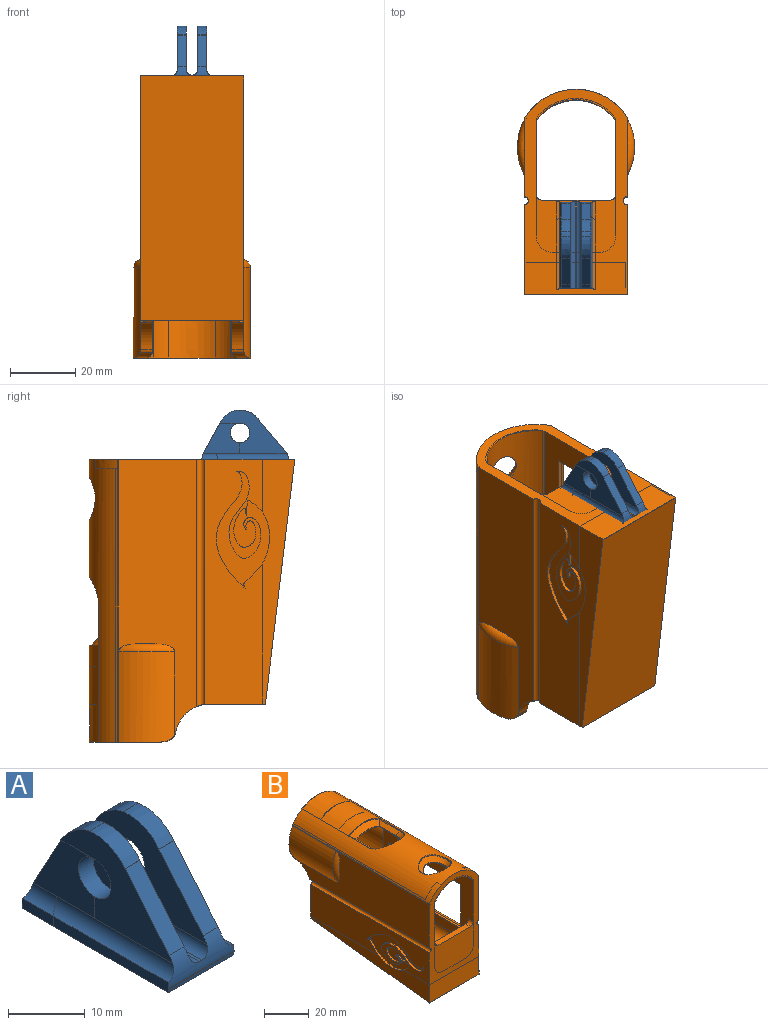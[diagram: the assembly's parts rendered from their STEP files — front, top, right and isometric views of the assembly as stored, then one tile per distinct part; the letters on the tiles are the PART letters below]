
ASSEMBLY  parts=2 mates=1
PART A: 46 faces, bbox 12.1x27.6x17 mm
  f0: extruded ~12.04x3.57mm, area 34.1mm2, adj f5,f6,f8,f10,f11,f12,f13,f14
  f1: plane 20.62x13.45mm, normal (-1,0,0), area 121.6mm2, adj f7,f8,f15,f16,f17,f22,f24,f28
  f2: plane 21.84x13.45mm, normal (1,0,0), area 173.4mm2, adj f9,f18,f20,f22,f23,f29,f30,f35
  f3: plane 23.73x13.5mm, normal (1,0,0), area 180.6mm2, adj f5,f15,f16,f17,f22,f24,f26,f31
  f4: plane 23.73x13.5mm, normal (-1,0,0), area 180.6mm2, adj f6,f18,f22,f23,f25,f29,f30,f35
  f5: bspline ~5x3.72mm, area 10.4mm2, adj f0,f3,f26,f41
  f6: bspline ~5x4.09mm, area 10.4mm2, adj f0,f4,f25,f40
  f7: plane 5.68x0mm, normal (0,0,-1), area 0mm2, adj f1,f8,f15,f42
  f8: plane 11.28x9.4mm, normal (-1,0,0), area 68.2mm2, adj f0,f1,f7,f14,f15,f28,f36,f41
  f9: plane 7.19x4.21mm, normal (1,0,0), area 16.3mm2, adj f2,f39,f40
  f10: plane 5.82x1.62mm, normal (1,0,0), area 9.3mm2, adj f0,f11,f12,f32,f39
  f11: plane 27.2x12.05mm, normal (0,0,-1), area 327.5mm2, adj f0,f10,f12,f13,f19,f32,f33,f37
  f12: cylinder r=10mm len=1.15mm, axis (0,0,1), area 0.4mm2, adj f0,f10,f11
  f13: cylinder r=10mm len=1.16mm, axis (0,0,-1), area 0.4mm2, adj f0,f11,f37
  f14: plane 4.2x0mm, normal (0,0,1), area 0mm2, adj f0,f8,f38
  f15: cylinder r=3mm len=6mm, axis (-1,0,0), area 51.8mm2, adj f1,f3,f7,f8,f36
  f16: extruded ~6.58x2.75mm, area 20.5mm2, adj f1,f3,f17,f44
  f17: plane 2.75x0.01mm, normal (0,-0.61,-0.8), area 0mm2, adj f1,f3,f16,f31
  f18: plane 2.75x0.01mm, normal (0,-0.61,-0.8), area 0mm2, adj f2,f4,f29,f35
  f19: cylinder r=5mm len=12.05mm, axis (-1,0,0), area 6mm2, adj f11,f21,f32,f33
  f20: cylinder r=2mm len=22.15mm, axis (0,-1,0), area 57mm2, adj f2,f22,f32,f39
  f21: plane 12.05x0.16mm, normal (0,-1,0), area 2mm2, adj f19,f22,f32,f33
  f22: cylinder r=6mm len=12.05mm, axis (1,0,0), area 33.2mm2, adj f1,f2,f3,f4,f20,f21,f23,f24
  f23: plane 9.73x8.15mm, normal (0,-0.77,0.64), area 34.9mm2, adj f2,f4,f22,f29
  f24: plane 9.73x8.15mm, normal (0,-0.77,0.64), area 34.9mm2, adj f1,f3,f22,f31
  f25: cylinder r=1.5mm len=26.67mm, axis (0,1,0), area 61.7mm2, adj f0,f4,f6,f22,f27,f34
  f26: cylinder r=1.5mm len=26.67mm, axis (0,1,0), area 61.7mm2, adj f0,f3,f5,f22,f27,f34
  f27: plane 22.48x0.5mm, normal (0,0,1), area 11.2mm2, adj f22,f25,f26,f34
  f28: cylinder r=2mm len=22.14mm, axis (0,1,0), area 56.7mm2, adj f1,f8,f22,f33,f38
  f29: plane 2.75x0.02mm, normal (0,0,1), area 0mm2, adj f2,f4,f18,f23
  f30: cylinder r=3mm len=6mm, axis (-1,0,0), area 51.8mm2, adj f2,f4
  f31: plane 2.75x0.02mm, normal (0,0,1), area 0mm2, adj f1,f3,f17,f24
  f32: plane 21.18x1.61mm, normal (1,0,0), area 34.1mm2, adj f10,f11,f19,f20,f21,f22
  f33: plane 21.18x1.62mm, normal (-1,0,0), area 34.1mm2, adj f11,f19,f21,f22,f28,f37
  f34: bspline ~5x0.5mm, area 2.1mm2, adj f0,f25,f26,f27
  f35: extruded ~6.58x2.75mm, area 20.5mm2, adj f2,f4,f18,f45
  f36: plane 3.31x0mm, normal (0,1,0), area 0mm2, adj f1,f8,f15
  f37: plane 5.82x1.62mm, normal (-1,0,0), area 9.3mm2, adj f0,f11,f13,f33,f38
  f38: cylinder r=2mm len=5.73mm, axis (0,-1,0), area 13.2mm2, adj f0,f14,f28,f37
  f39: cylinder r=2mm len=5.72mm, axis (0,-1,0), area 12.8mm2, adj f0,f9,f10,f20
  f40: plane 9.16x4.93mm, normal (0,0.88,0.47), area 28.5mm2, adj f0,f2,f4,f6,f9,f43
  f41: plane 9.13x4.91mm, normal (0,0.88,0.47), area 28.5mm2, adj f0,f3,f5,f8,f42
  f42: cylinder r=9mm len=3.74mm, axis (-1,0,0), area 14.7mm2, adj f1,f3,f7,f8,f41,f44
  f43: cylinder r=9mm len=3.74mm, axis (-1,0,0), area 14.7mm2, adj f2,f4,f40,f45
  f44: cylinder r=5mm len=2.75mm, axis (-1,0,0), area 4.7mm2, adj f1,f3,f16,f42
  f45: cylinder r=5mm len=2.75mm, axis (-1,0,0), area 4.7mm2, adj f2,f4,f35,f43
PART B: 118 faces, bbox 48.8x101.4x78.2 mm
  f0: plane 85.08x35.34mm, normal (-1,0,0), area 1245.9mm2, adj f1,f2,f6,f7,f8,f14,f19,f59
  f1: cylinder r=14.7mm len=29.6mm, axis (0,-1,0), area 476.1mm2, adj f0,f2,f59,f61,f112
  f2: plane 16.17x2.49mm, normal (0,1,0), area 27.6mm2, adj f0,f1,f112
  f3: plane 96.6x34.13mm, normal (1,0,0), area 527.4mm2, adj f5,f6,f8,f14,f20,f22,f46,f52
  f4: plane 75.02x17.53mm, normal (1,0,0), area 955.8mm2, adj f5,f6,f16,f19,f71,f78,f79,f81
  f5: cylinder r=1.25mm len=7.65mm, axis (0,-1,0), area 28mm2, adj f3,f4,f6,f81
  f6: plane 52.91x31.41mm, normal (0,-1,0), area 482.3mm2, adj f0,f3,f4,f5,f9,f10,f12,f20
  f7: cylinder r=16.78mm len=3.18mm, axis (-1,0,0), area 0mm2, adj f0,f19,f67,f71
  f8: cylinder r=12.84mm len=3.5mm, axis (1,0,0), area 6.8mm2, adj f0,f3,f66,f67,f71
  f9: plane 75.02x17.79mm, normal (-1,0,0), area 1028.1mm2, adj f6,f15,f19,f47,f50,f70
  f10: plane 96.6x33.99mm, normal (-1,0,0), area 1509.7mm2, adj f6,f11,f13,f31,f44,f53,f54,f61
  f11: cylinder r=12.84mm len=3.5mm, axis (1,0,0), area 6.9mm2, adj f10,f12,f68,f69,f70
  f12: plane 85.08x35.34mm, normal (1,0,0), area 2349.9mm2, adj f6,f11,f13,f21,f26,f47,f60,f62
  f13: cylinder r=10.69mm len=8.11mm, axis (1,0,0), area 37.7mm2, adj f10,f12,f64,f68
  f14: cylinder r=10.69mm len=8.11mm, axis (1,0,0), area 37.7mm2, adj f0,f3,f65,f66
  f15: plane 75.52x10.51mm, normal (-1,0,0), area 387.4mm2, adj f9,f24,f50,f84,f86,f87
  f16: offset ~81.78x17.23mm, area 230.7mm2, adj f4,f17,f37,f82
  f17: bspline ~75x5mm, area 103.7mm2, adj f16,f49,f83,f85
  f18: plane 72.01x14.4mm, normal (0,0,1), area 1037mm2, adj f19,f72,f73,f115
  f19: plane 31.41x17.58mm, normal (0,1,0), area 150.7mm2, adj f0,f4,f7,f9,f18,f47,f71,f73
  f20: cylinder r=18.45mm len=86.6mm, axis (0,-1,0), area 1936.6mm2, adj f3,f6,f23,f32,f33,f34,f36,f38
  f21: cylinder r=14.7mm len=29.6mm, axis (0,-1,0), area 478.5mm2, adj f12,f26,f60,f61,f107
  f22: cylinder r=17.94mm len=27.6mm, axis (0,-1,0), area 495.5mm2, adj f3,f52,f57,f58,f61
  f23: extruded ~83.6x0.64mm, area 64.4mm2, adj f20,f44,f45,f61
  f24: plane 31.47x10.01mm, normal (0,-1,0), area 310.5mm2, adj f6,f15,f37,f49,f85,f86
  f25: plane 12.81x2.24mm, normal (-0.54,0,0.84), area 30.9mm2, adj f28,f30,f39,f89
  f26: plane 16.17x2.48mm, normal (0,1,0), area 27.4mm2, adj f12,f21,f107
  f27: plane 12.82x2.24mm, normal (0.54,0,0.84), area 30.9mm2, adj f28,f30,f33,f101
  f28: bspline ~19.04x8.2mm, area 61.9mm2, adj f25,f27,f32,f88
  f29: bspline ~15.54x13.39mm, area 112.7mm2, adj f38,f99
  f30: bspline ~20.52x5.77mm, area 58.2mm2, adj f25,f27,f35,f91
  f31: cylinder r=17.94mm len=27.6mm, axis (0,-1,0), area 494.6mm2, adj f10,f53,f54,f55,f61
  f32: bspline ~19.56x8.2mm, area 14.4mm2, adj f20,f28,f33,f39
  f33: plane 12.81x0.43mm, normal (0.85,0,0.53), area 6.4mm2, adj f20,f27,f32,f34
  f34: plane 0.44x0.27mm, normal (0.75,-0.5,0.43), area 0mm2, adj f20,f33,f35
  f35: bspline ~19.54x3.23mm, area 10.2mm2, adj f30,f34,f36,f42
  f36: plane 0.43x0.27mm, normal (-0.75,-0.5,0.44), area 0mm2, adj f20,f35,f39
  f37: bspline ~4x0.53mm, area 2mm2, adj f6,f16,f24,f49
  f38: bspline ~15.96x13.39mm, area 23.3mm2, adj f20,f29
  f39: plane 12.81x0.42mm, normal (-0.85,0,0.53), area 6.4mm2, adj f20,f25,f32,f36
  f40: extruded ~19.54x2.8mm, area 0.3mm2, adj f20,f41,f48
  f41: offset ~20.38x12.53mm, area 237.2mm2, adj f20,f40,f42
  f42: offset ~20.38x11.46mm, area 133.7mm2, adj f20,f35,f41
  f43: plane 0.5x0.27mm, normal (0,-1,0), area 0.1mm2, adj f6,f44
  f44: cylinder r=0.61mm len=86.6mm, axis (0,-1,0), area 24.1mm2, adj f10,f23,f43,f45,f61
  f45: extruded ~7.47x6.73mm, area 30.5mm2, adj f6,f20,f23,f44
  f46: extruded ~7.54x6.86mm, area 31mm2, adj f3,f6,f20
  f47: plane 14.57x8.51mm, normal (0,1,0), area 56.3mm2, adj f9,f12,f19,f69,f70,f72
  f48: extruded ~19.54x11.49mm, area 234.9mm2, adj f20,f40,f56
  f49: bspline ~3.89x0.53mm, area 1.9mm2, adj f17,f24,f37
  f50: extruded ~35.83x15.97mm, area 169mm2, adj f9,f15,f51
  f51: plane 36.43x16.64mm, normal (-1,0,0), area 295.7mm2, adj f50
  f52: torus R=15.44mm, axis (0,-1,0), area 0mm2, adj f3,f22
  f53: torus R=15.44mm, axis (0,-1,0), area 0mm2, adj f10,f31
  f54: bspline ~0.72x0.51mm, area 0.1mm2, adj f10,f31,f55,f64
  f55: bspline ~3.69x1.65mm, area 0.4mm2, adj f31,f54,f62
  f56: bspline ~19.54x2.8mm, area 2mm2, adj f20,f48,f61
  f57: bspline ~3.69x1.65mm, area 0.4mm2, adj f22,f58,f63
  f58: bspline ~0.72x0.51mm, area 0.1mm2, adj f3,f22,f57,f65
  f59: bspline ~3.63x1.74mm, area 0.4mm2, adj f0,f1,f63
  f60: bspline ~3.63x1.74mm, area 0.4mm2, adj f12,f21,f62
  f61: plane 35.85x22.18mm, normal (0,1,0), area 196.4mm2, adj f1,f3,f10,f20,f21,f22,f23,f31
  f62: cylinder r=5.1mm len=5.12mm, axis (1,0,0), area 14.7mm2, adj f12,f55,f60,f61,f64
  f63: cylinder r=5.1mm len=5.12mm, axis (-1,0,0), area 14.7mm2, adj f0,f57,f59,f61,f65
  f64: cylinder r=2.1mm len=3.72mm, axis (-1,0,0), area 4.5mm2, adj f10,f12,f13,f54,f62
  f65: cylinder r=2.1mm len=3.72mm, axis (-1,0,0), area 4.5mm2, adj f0,f3,f14,f58,f63
  f66: plane 3.5x0mm, normal (0,-0.4,-0.92), area 0mm2, adj f0,f3,f8,f14
  f67: plane 3.17x0mm, normal (0,0.2,0.98), area 0mm2, adj f0,f7,f8,f71
  f68: plane 3.5x0mm, normal (0,-0.4,-0.92), area 0mm2, adj f10,f11,f12,f13
  f69: plane 3.24x0.01mm, normal (0,0.2,0.98), area 0mm2, adj f11,f12,f47,f70
  f70: cylinder r=1.25mm len=75.77mm, axis (0,-1,0), area 283.8mm2, adj f6,f9,f10,f11,f47,f69
  f71: cylinder r=1.25mm len=21.42mm, axis (0,-1,0), area 79.9mm2, adj f3,f4,f7,f8,f19,f67,f78
  f72: cylinder r=5mm len=72.02mm, axis (0,1,0), area 565.6mm2, adj f12,f18,f47,f115
  f73: cylinder r=5mm len=72.01mm, axis (0,-1,0), area 565.6mm2, adj f0,f18,f19,f115
  f74: plane 24x1mm, normal (0,1,0), area 24mm2, adj f0,f75,f77,f81
  f75: plane 46x1mm, normal (0,0,1), area 46mm2, adj f0,f74,f76,f79
  f76: plane 24x1mm, normal (0,-1,0), area 24mm2, adj f0,f75,f77,f78
  f77: plane 46x1mm, normal (0,0,-1), area 46mm2, adj f0,f74,f76,f80
  f78: cylinder r=2.5mm len=29mm, axis (0,0,-1), area 98.5mm2, adj f3,f4,f71,f76,f79,f80
  f79: cylinder r=2.5mm len=51mm, axis (0,-1,0), area 190.5mm2, adj f4,f75,f78,f81
  f80: cylinder r=2.5mm len=51mm, axis (0,1,0), area 190.5mm2, adj f3,f77,f78,f81
  f81: cylinder r=2.5mm len=29mm, axis (0,0,1), area 98.5mm2, adj f3,f4,f5,f74,f79,f80
  f82: extruded ~33.42x4.99mm, area 33.2mm2, adj f16,f83,f84,f87
  f83: extruded ~40.71x5.86mm, area 40.9mm2, adj f17,f82,f84,f85
  f84: plane 74.89x31.47mm, normal (0,0.12,-0.99), area 2371.5mm2, adj f15,f82,f83,f85,f86,f87
  f85: plane 2.8x1.91mm, normal (1,0,0), area 1.5mm2, adj f17,f24,f83,f84,f86
  f86: plane 31.47x0.12mm, normal (0,0.11,-0.99), area 3.8mm2, adj f15,f24,f84,f85
  f87: plane 31.4x1.01mm, normal (0,1,0), area 31.4mm2, adj f15,f19,f82,f84
  f88: bspline ~14.57x6.37mm, area 8.7mm2, adj f28,f89,f101,f102
  f89: plane 10.47x0.35mm, normal (-0.88,0,0.48), area 4.2mm2, adj f25,f88,f90,f102
  f90: plane 0.36x0.19mm, normal (-0.78,0.5,0.38), area 0mm2, adj f89,f91,f102
  f91: bspline ~14.69x2.19mm, area 6mm2, adj f30,f90,f92,f103
  f92: plane 0.36x0.19mm, normal (0.77,0.5,0.39), area 0mm2, adj f91,f101,f102
  f93: bspline ~14.56x2.13mm, area 6mm2, adj f94,f100,f104,f106
  f94: plane 0.36x0.18mm, normal (-0.77,-0.5,0.39), area 0mm2, adj f93,f95,f102
  f95: bspline ~0.36x0.18mm, area 0mm2, adj f94,f96,f102,f106
  f96: plane 14.56x2.13mm, normal (0,-1,0), area 6mm2, adj f95,f97,f105,f106
  f97: plane 0.36x0.18mm, normal (0.77,0.5,0.39), area 0mm2, adj f96,f100,f102
  f98: plane 24.4x6.32mm, normal (0,-1,0), area 11.2mm2, adj f6,f102,f109,f110
  f99: bspline ~11.17x9.74mm, area 13.2mm2, adj f29,f102
  f100: bspline ~0.36x0.18mm, area 0mm2, adj f93,f97,f102,f106
  f101: plane 10.47x0.35mm, normal (0.88,0,0.48), area 4.2mm2, adj f27,f88,f92,f102
  f102: cylinder r=14.89mm len=86.6mm, axis (0,1,0), area 1596.8mm2, adj f61,f88,f89,f90,f92,f94,f95,f97
  f103: offset ~15.45x11.26mm, area 130.4mm2, adj f91,f102,f104
  f104: offset ~15.36x12.44mm, area 170mm2, adj f93,f102,f103
  f105: extruded ~14.2x11.59mm, area 170.9mm2, adj f61,f96,f102
  f106: extruded ~14.56x1.76mm, area 0.2mm2, adj f93,f95,f96,f100
  f107: plane 83.6x1.17mm, normal (0.8,0,-0.6), area 72.1mm2, adj f12,f21,f26,f61,f102,f108
  f108: plane 3x0.42mm, normal (0.8,0,-0.6), area 1.6mm2, adj f12,f102,f107,f109
  f109: plane 0.66x0.32mm, normal (0,-1,0), area 0.1mm2, adj f6,f98,f108
  f110: plane 0.66x0.32mm, normal (0,-1,0), area 0.1mm2, adj f6,f98,f111
  f111: plane 3x0.42mm, normal (-0.8,0,-0.6), area 1.6mm2, adj f0,f102,f110,f112
  f112: plane 83.6x1.25mm, normal (-0.8,0,-0.6), area 74.8mm2, adj f0,f1,f2,f61,f102,f111
  f113: plane 20.4x3mm, normal (0,0,1), area 61.2mm2, adj f114,f115,f116,f117
  f114: plane 24.4x17.9mm, normal (0,-1,0), area 379.1mm2, adj f6,f113,f116,f117
  f115: plane 24.4x17.9mm, normal (0,1,0), area 379mm2, adj f0,f12,f18,f72,f73,f113,f116,f117
  f116: cylinder r=2mm len=3mm, axis (0,-1,0), area 9.4mm2, adj f0,f113,f114,f115
  f117: cylinder r=2mm len=3mm, axis (0,1,0), area 9.4mm2, adj f12,f113,f114,f115
PLACE A t=(0,-11.5,0)mm
PLACE B rot(axis=(-1,0,0),90deg) t=(-50.28,-18.26,-50.93)mm
MATE planar B.f114 <-> A.f27  axis (0,0,1) through (0,5.57,3)mm
